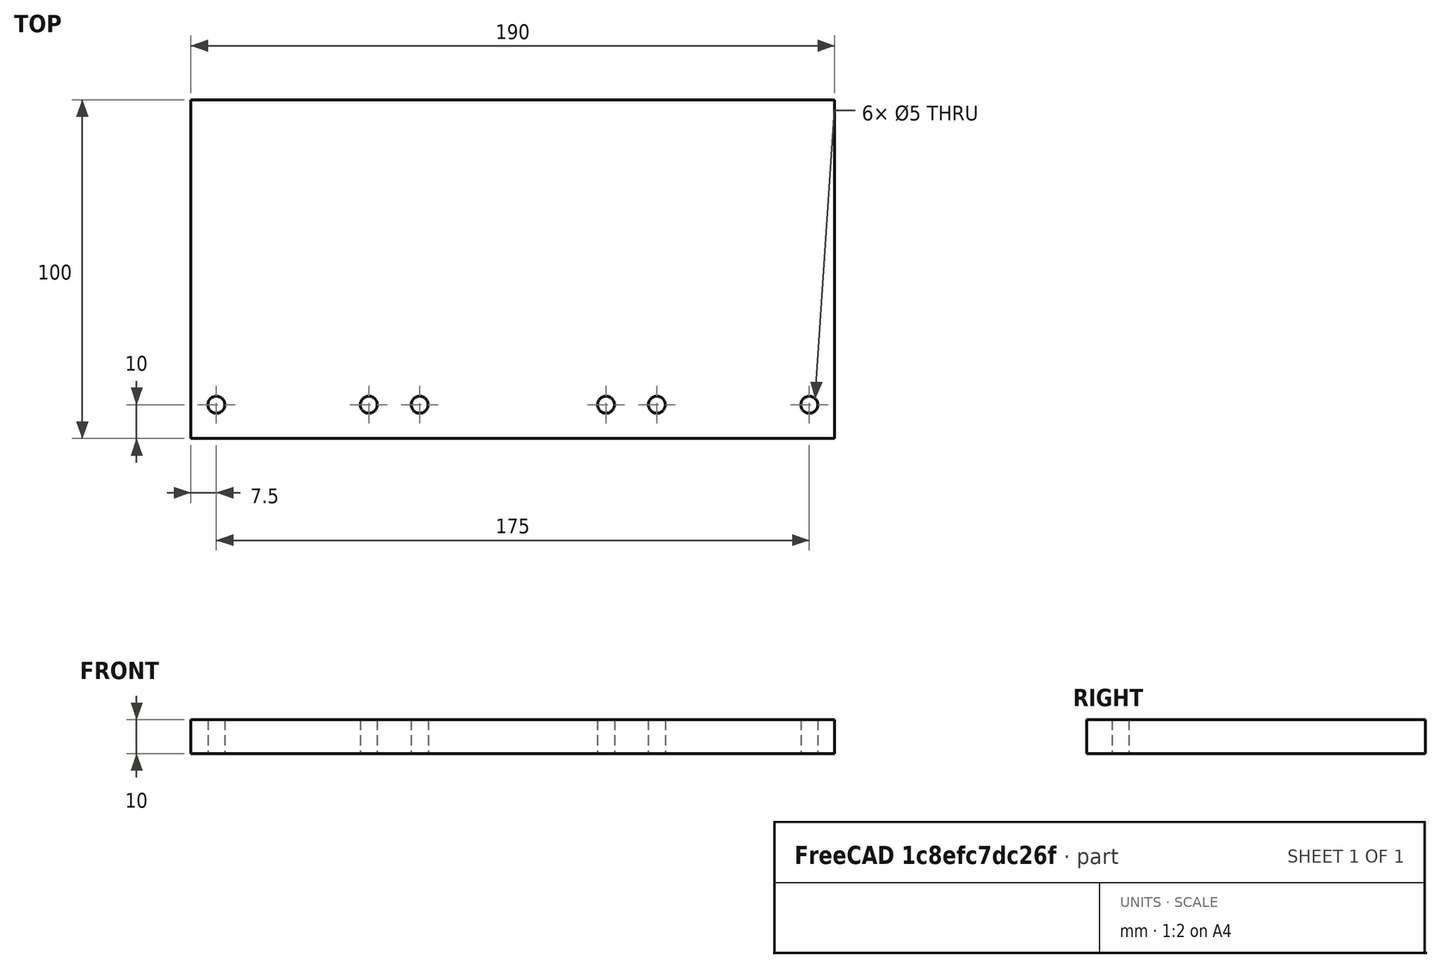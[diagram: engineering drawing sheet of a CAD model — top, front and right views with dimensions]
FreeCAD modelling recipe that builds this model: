
FCSTD DOCUMENT  (FreeCAD 0.17R13528 (Git))
Label: plate9
License: All rights reserved
LicenseURL: http://en.wikipedia.org/wiki/All_rights_reserved
objects: TechDraw::DrawViewDimension×16, PartDesign::LinearPattern×4, Sketcher::SketchObject×3, TechDraw::DrawProjGroupItem×3, PartDesign::Hole×2, PartDesign::Pad×1, PartDesign::Body×1, TechDraw::DrawSVGTemplate×1, TechDraw::DrawProjGroup×1, TechDraw::DrawViewAnnotation×1, TechDraw::DrawPage×1
note: 14 computed .brp shape members not serialized (recipe doc carries the construction recipe); baked Part::Feature solids carry a one-line shape summary decoded from their .brp

FEATURE [Sketcher::SketchObject] Sketch
  MapMode = 5
  Support = -> [XY_Plane]
  sketch-geometry (4):
    g0: LineSegment StartX=0 StartY=0 StartZ=0 EndX=190 EndY=0 EndZ=0
    g1: LineSegment StartX=190 StartY=0 StartZ=0 EndX=190 EndY=100 EndZ=0
    g2: LineSegment StartX=190 StartY=100 StartZ=0 EndX=0 EndY=100 EndZ=0
    g3: LineSegment StartX=0 StartY=100 StartZ=0 EndX=0 EndY=0 EndZ=0
  constraints (11):
    c: Coincident(g0,g1)
    c: Coincident(g1,g2)
    c: Coincident(g2,g3)
    c: Coincident(g3,g0)
    c: Horizontal(g0)
    c: Horizontal(g2)
    c: Vertical(g1)
    c: Vertical(g3)
    c: Coincident(g0,g-1)
    c: DistanceY(g3,g3) = 100
    c: DistanceX(g0,g0) = 190
FEATURE [PartDesign::Pad] Pad
  Length = 10
  Length2 = 100
  Profile = -> Sketch
  Type = 0
FEATURE [Sketcher::SketchObject] Sketch001
  MapMode = 5
  Placement = pos=(0,0,10) rot=(0,0,1;0rad)
  Support = -> [Pad]
  sketch-geometry (1):
    g0: Circle CenterX=7.5 CenterY=10 CenterZ=0 NormalX=0 NormalY=0 NormalZ=1 AngleXU=0 Radius=5.61313
  constraints (2):
    c: Distance(g0,g-1) = 10
    c: Distance(g0,g-2) = 7.5
FEATURE [PartDesign::Hole] Hole
  BaseFeature = -> Pad
  Depth = 25
  DepthType = 1
  Diameter = 5
  DrillPoint = 0
  DrillPointAngle = 118
  HoleCutCountersinkAngle = 90
  HoleCutDepth = 0
  HoleCutDiameter = 6
  HoleCutType = 0
  ModelActualThread = false
  Profile = -> Sketch001
  Tapered = false
  TaperedAngle = 90
  ThreadAngle = 60
  ThreadClass = 0
  ThreadCutOffInner = 0.108253
  ThreadCutOffOuter = 0.216506
  ThreadDirection = 1
  ThreadFit = 0
  ThreadPitch = 1
  ThreadSize = 7
  ThreadType = 1
  Threaded = true
FEATURE [Sketcher::SketchObject] Sketch002
  MapMode = 5
  Placement = pos=(0,0,10) rot=(0,0,1;0rad)
  Support = -> [Hole]
  sketch-geometry (1):
    g0: Circle CenterX=52.5 CenterY=10 CenterZ=0 NormalX=0 NormalY=0 NormalZ=1 AngleXU=0 Radius=4.75738
  constraints (2):
    c: Distance(g0,g-1) = 10
    c: Distance(g0,g-2) = 52.5
FEATURE [PartDesign::Hole] Hole001
  BaseFeature = -> Hole
  Depth = 25
  DepthType = 1
  Diameter = 5
  DrillPoint = 0
  DrillPointAngle = 118
  HoleCutCountersinkAngle = 90
  HoleCutDepth = 0
  HoleCutDiameter = 6
  HoleCutType = 0
  ModelActualThread = false
  Profile = -> Sketch002
  Tapered = false
  TaperedAngle = 90
  ThreadAngle = 60
  ThreadClass = 0
  ThreadCutOffInner = 0.108253
  ThreadCutOffOuter = 0.216506
  ThreadDirection = 1
  ThreadFit = 0
  ThreadPitch = 1
  ThreadSize = 7
  ThreadType = 1
  Threaded = true
FEATURE [PartDesign::LinearPattern] LinearPattern
  BaseFeature = -> Hole001
  Direction = -> Sketch002 [H_Axis]
  Length = 15
  Occurrences = 2
  Originals = -> [Hole001]
FEATURE [PartDesign::LinearPattern] LinearPattern001
  BaseFeature = -> LinearPattern
  Direction = -> Sketch002 [H_Axis]
  Length = 70
  Occurrences = 2
  Originals = -> [Hole001]
FEATURE [PartDesign::LinearPattern] LinearPattern002
  BaseFeature = -> LinearPattern001
  Direction = -> Sketch002 [H_Axis]
  Length = 85
  Occurrences = 2
  Originals = -> [Hole001]
FEATURE [PartDesign::LinearPattern] LinearPattern003
  BaseFeature = -> LinearPattern002
  Direction = -> Sketch002 [H_Axis]
  Length = 130
  Occurrences = 2
  Originals = -> [Hole001]
FEATURE [PartDesign::Body] Body
  Group = -> [Sketch,Pad,Sketch001,Hole,Sketch002,Hole001,LinearPattern,LinearPattern001,LinearPattern002,LinearPattern003]
  Origin = -> Origin
  Tip = -> LinearPattern003
FEATURE [TechDraw::DrawSVGTemplate] Template
  EditableTexts = Designed_by_Name=Lukas Winter; FC-Date=11.10.2018; FC-SC=1:2; FC-SH=1/1; FC-Title=COSI measure v1.0; Subtitle=Mechanical assembly - plate 9
  Height = 210
  Orientation = 1
  Width = 297
FEATURE [TechDraw::DrawProjGroupItem] ProjItem  label="Front"
  CoarseView = false
  Direction = (0,-1,0)
  Focus = 100
  HardHidden = false
  IsoCount = 0
  IsoHidden = false
  IsoVisible = false
  LockPosition = false
  Perspective = false
  Rotation = 0
  RotationVector = (1,0,0)
  ScaleType = 0
  SeamHidden = false
  SeamVisible = false
  SmoothHidden = false
  SmoothVisible = false
  Source = -> [Body]
  Type = 0
  X = 30.0305
  Y = -51.8836
FEATURE [TechDraw::DrawProjGroupItem] ProjItem001  label="Top"
  CoarseView = false
  Direction = (0,0,1)
  Focus = 100
  HardHidden = false
  IsoCount = 0
  IsoHidden = false
  IsoVisible = false
  LockPosition = false
  Perspective = false
  Rotation = 0
  RotationVector = (1,0,0)
  ScaleType = 0
  SeamHidden = false
  SeamVisible = false
  SmoothHidden = false
  SmoothVisible = false
  Source = -> [Body]
  Type = 4
  X = 0
  Y = 65
FEATURE [TechDraw::DrawProjGroupItem] ProjItem002  label="Left"
  CoarseView = false
  Direction = (-1,0,0)
  Focus = 100
  HardHidden = false
  IsoCount = 0
  IsoHidden = false
  IsoVisible = false
  LockPosition = false
  Perspective = false
  Rotation = 0
  RotationVector = (0,1,0)
  ScaleType = 2
  SeamHidden = false
  SeamVisible = false
  SmoothHidden = false
  SmoothVisible = false
  Source = -> [Body]
  Type = 1
  X = -110
  Y = 0
FEATURE [TechDraw::DrawProjGroup] ProjGroup
  Anchor = -> ProjItem
  AutoDistribute = true
  CubeDirs = (6) [(0,0,-1),(-2.44929e-16,-1,0),(-1,2.44929e-16,0),(2.44929e-16,1,0),(1,-2.44929e-16,0),(0,0,1)]
  CubeRotations = (6) [(1,2.44929e-16,0),(1,2.44929e-16,0),(-2.44929e-16,1,0),(-1,-2.44929e-16,0),(2.44929e-16,-1,0),(1,2.44929e-16,0)]
  LockPosition = false
  ProjectionType = 2
  Rotation = 0
  Scale = 0.5
  ScaleType = 1
  Source = -> [Body]
  Views = -> [ProjItem,ProjItem001,ProjItem002]
  X = 194.543
  Y = 93.9803
  spacingX = 15
  spacingY = 15
FEATURE [TechDraw::DrawViewDimension] Dimension
  FormatSpec = %.2f
  LockPosition = false
  MeasureType = 1
  References2D = -> [ProjItem001]
  Rotation = 0
  ScaleType = 0
  Type = 5
  X = 0
  Y = 0
FEATURE [TechDraw::DrawViewDimension] Dimension001 .. Dimension005  x5 (patterned run collapsed; names and placements below)
  FormatSpec = %.2f
  LockPosition = false
  MeasureType = 1
  References2D = -> [ProjItem001]
  Rotation = 0
  ScaleType = 0
  Type = 5
  X = 0
  Y = 0
FEATURE [TechDraw::DrawViewDimension] Dimension006
  FormatSpec = %.2f
  LockPosition = false
  MeasureType = 1
  References2D = -> [ProjItem]
  Rotation = 0
  ScaleType = 0
  Type = 2
  X = -62.6185
  Y = -0.312571
FEATURE [TechDraw::DrawViewDimension] Dimension007
  FormatSpec = %.2f
  LockPosition = false
  MeasureType = 1
  References2D = -> [ProjItem]
  Rotation = 0
  ScaleType = 0
  Type = 1
  X = 5.45288
  Y = -22.4269
FEATURE [TechDraw::DrawViewDimension] Dimension008
  FormatSpec = %.2f
  LockPosition = false
  MeasureType = 1
  References2D = -> [ProjItem002]
  Rotation = 0
  ScaleType = 0
  Type = 1
  X = 0.710011
  Y = 13.0169
FEATURE [TechDraw::DrawViewDimension] Dimension009
  FormatSpec = %.2f
  LockPosition = false
  MeasureType = 1
  References2D = -> [ProjItem001]
  Rotation = 0
  ScaleType = 0
  Type = 2
  X = -75.3634
  Y = -4.88772
FEATURE [TechDraw::DrawViewDimension] Dimension010
  FormatSpec = %.2f
  LockPosition = false
  MeasureType = 1
  References2D = -> [ProjItem001]
  Rotation = 0
  ScaleType = 0
  Type = 1
  X = -60.1239
  Y = -5.02205
FEATURE [TechDraw::DrawViewDimension] Dimension011
  FormatSpec = %.2f
  LockPosition = false
  MeasureType = 1
  References2D = -> [ProjItem001]
  Rotation = 0
  ScaleType = 0
  Type = 1
  X = -30.679
  Y = -37.1605
FEATURE [TechDraw::DrawViewDimension] Dimension012
  FormatSpec = %.2f
  LockPosition = false
  MeasureType = 1
  References2D = -> [ProjItem001]
  Rotation = 0
  ScaleType = 0
  Type = 1
  X = -2.18759
  Y = -44.798
FEATURE [TechDraw::DrawViewDimension] Dimension013
  FormatSpec = %.2f
  LockPosition = false
  MeasureType = 1
  References2D = -> [ProjItem001]
  Rotation = 0
  ScaleType = 0
  Type = 1
  X = 63.8911
  Y = -2.74884
FEATURE [TechDraw::DrawViewDimension] Dimension014
  FormatSpec = %.2f
  LockPosition = false
  MeasureType = 1
  References2D = -> [ProjItem001]
  Rotation = 0
  ScaleType = 0
  Type = 1
  X = 32.7339
  Y = -37.3906
FEATURE [TechDraw::DrawViewDimension] Dimension015
  FormatSpec = %.2f
  LockPosition = false
  MeasureType = 1
  References2D = -> [ProjItem001]
  Rotation = 0
  ScaleType = 0
  Type = 1
  X = 32.2593
  Y = -49.4241
FEATURE [TechDraw::DrawViewAnnotation] Annotation
  Font = osifont
  LineSpace = 80
  LockPosition = false
  MaxWidth = -1
  Rotation = 0
  ScaleType = 0
  Text = Note: For the holes (d=5mm) make a thread M6. | Alternatively you can also make a through hole | (d=6.6mm) and use a longer M6 screw together  | with a screw nut on the other end.
  TextSize = 4
  TextStyle = 0
  X = 67.9536
  Y = 183.541
FEATURE [TechDraw::DrawPage] Page
  KeepUpdated = true
  ProjectionType = 0
  Template = -> Template
  Views = -> [ProjGroup,Dimension,Dimension001,Dimension002,Dimension003,Dimension004,Dimension005,Dimension006,Dimension007,Dimension008,Dimension009,Dimension010,Dimension011,Dimension012,Dimension013,Dimension014,Dimension015,Annotation]
